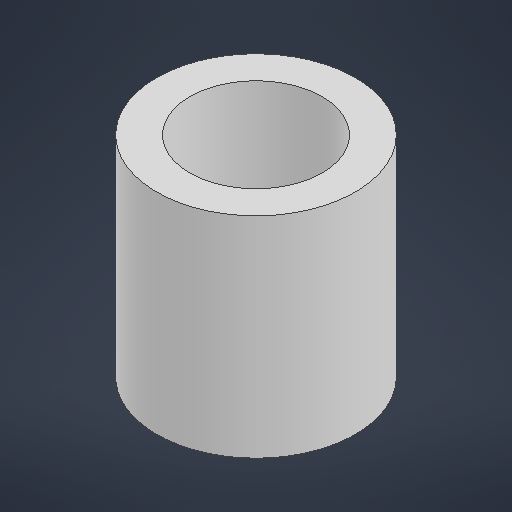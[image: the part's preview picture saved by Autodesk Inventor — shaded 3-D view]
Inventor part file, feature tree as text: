
AUTODESK INVENTOR PART (.ipt)
format: ipt  version: 2025.1 (Build 291241000, 241)  size: 157,184 bytes
history: native  units: mm
features: extrude x1, sketch x1
ambient origin geometry x8: Origin, YZ Plane, XZ Plane, XY Plane, X Axis, Y Axis, Z Axis, Center Point
bodies: Solid1 (feature_tree)
feature tree (2):
  extrude  "Extrusion1"  Depth=8.25mm
  sketch  "Sketch1"  dims[d0=7.8mm d1=5.2mm d2=8.25mm d3=0.0mm]
